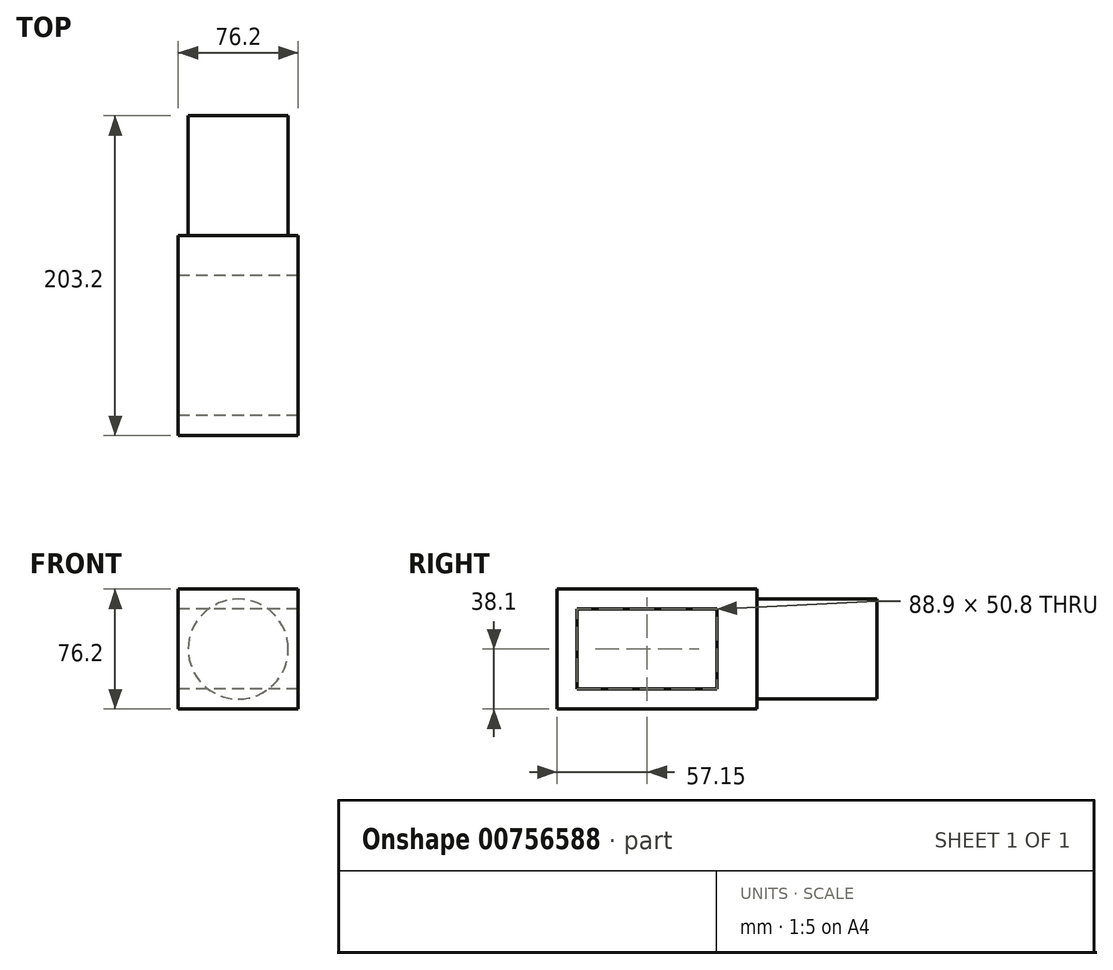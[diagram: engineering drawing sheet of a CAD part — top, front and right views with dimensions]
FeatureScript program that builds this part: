
annotation { "Feature Type Name" : "Feature", "Feature Type Description" : "" }
export const myFeature = defineFeature(function(context is Context, id is Id, definition is map)
    precondition{}
    {
        {
            var Q0;
            Q0=qCreatedBy(makeId("Right.planeOp"),FACE);
            var sketch = newSketch(context, id + "F0", { "sketchPlane" : qUnion([Q0])});
            skLineSegment(sketch, "E0.bottom", {"start": v(63.5, -38.1) * mm, "end": v(-63.5, -38.1) * mm});
            skLineSegment(sketch, "E0.top", {"start": v(63.5, 38.1) * mm, "end": v(-63.5, 38.1) * mm});
            skLineSegment(sketch, "E0.left", {"start": v(63.5, -38.1) * mm, "end": v(63.5, 38.1) * mm});
            skLineSegment(sketch, "E0.right", {"start": v(-63.5, -38.1) * mm, "end": v(-63.5, 38.1) * mm});
            skPoint(sketch, "E0.middle", {"position": v(0, 0) * mm});
            skSolve(sketch);
        }
        {
            var Q0;
            Q0 = qSketchRegion(id + "F0", true);
            extrude(context, id + "F1", {"entities" : qUnion([Q0]), "depth" : 76.2 * mm, "offsetDistance" : 25.4 * mm});
        }
        {
            var Q0;
            Q0=makeQuery(id+"F1.opExtrude","SWEPT_FACE",FACE,{"disambiguationData":[OSD([sQuery(id+"F0.wireOp",EDGE,"E0.left")])]});
            var sketch = newSketch(context, id + "F2", { "sketchPlane" : qUnion([Q0])});
            skLineSegment(sketch, "E1.0", {"start": v(0, -38.1) * mm, "end": v(0, 38.1) * mm});
            skLineSegment(sketch, "E2.0", {"start": v(-76.2, -38.1) * mm, "end": v(0, -38.1) * mm});
            skLineSegment(sketch, "E3.0", {"start": v(-76.2, -38.1) * mm, "end": v(-76.2, 38.1) * mm});
            skLineSegment(sketch, "E4.0", {"start": v(-76.2, 38.1) * mm, "end": v(0, 38.1) * mm});
            skCircle(sketch, "E5", {"center": v(-38.1, 0) * mm, "radius": 38.1 * mm});
            skPoint(sketch, "E5.first.point", {"position": v(0, 0) * mm});
            skPoint(sketch, "E5.second.point", {"position": v(-76.2, 0) * mm});
            skPoint(sketch, "E5.third.point", {"position": v(-38.1, -38.1) * mm});
            skCircle(sketch, "E6.0", {"center": v(-38.1, 0) * mm, "radius": 31.75 * mm});
            skSolve(sketch);
        }
        {
            var Q0;
            Q0=makeQuery(id+"F2.imprint","IMPRINT",FACE,{"disambiguationData":[TD([[makeQuery(id+"F2.imprint","IMPRINT",EDGE,{"derivedFrom":sQuery(id+"F2.wireOp",EDGE,"E6.0")}),1.0]])]});
            extrude(context, id + "F3", {"entities" : qUnion([Q0]), "operationType" : NewBodyOperationType.ADD, "depth" : 76.2 * mm, "offsetDistance" : 25.4 * mm});
        }
        {
            var Q0;
            Q0=makeQuery(id+"F1.opExtrude","CAP_FACE",FACE,{"disambiguationData":[OSD([sQuery(id+"F0.wireOp",EDGE,"E0.bottom"),sQuery(id+"F0.wireOp",EDGE,"E0.top"),sQuery(id+"F0.wireOp",EDGE,"E0.left"),sQuery(id+"F0.wireOp",EDGE,"E0.right")])],"isStart":true});
            var sketch = newSketch(context, id + "F4", { "sketchPlane" : qUnion([Q0])});
            skLineSegment(sketch, "E7.0", {"start": v(-63.5, -38.1) * mm, "end": v(-63.5, 38.1) * mm});
            skLineSegment(sketch, "E8.0", {"start": v(63.5, -38.1) * mm, "end": v(63.5, 38.1) * mm});
            skLineSegment(sketch, "E9.0", {"start": v(-63.5, -38.1) * mm, "end": v(63.5, -38.1) * mm});
            skLineSegment(sketch, "E10.0", {"start": v(-63.5, 38.1) * mm, "end": v(63.5, 38.1) * mm});
            skLineSegment(sketch, "E11", {"start": v(-38.1, 25.4) * mm, "end": v(-38.1, -25.4) * mm});
            skLineSegment(sketch, "E12", {"start": v(-38.1, -25.4) * mm, "end": v(50.8, -25.4) * mm});
            skLineSegment(sketch, "E13", {"start": v(50.8, -25.4) * mm, "end": v(50.8, 25.4) * mm});
            skLineSegment(sketch, "E14", {"start": v(50.8, 25.4) * mm, "end": v(-38.1, 25.4) * mm});
            skSolve(sketch);
        }
        {
            var Q0;
            Q0=makeQuery(id+"F4.imprint","IMPRINT",FACE,{"disambiguationData":[TD([[makeQuery(id+"F4.imprint","IMPRINT",EDGE,{"derivedFrom":sQuery(id+"F4.wireOp",EDGE,"E11")}),1.0]])]});
            extrude(context, id + "F5", {"entities" : qUnion([Q0]), "operationType" : NewBodyOperationType.REMOVE, "endBound" : BoundingType.THROUGH_ALL, "oppositeDirection" : true, "depth" : 25.4 * mm, "offsetDistance" : 25.4 * mm});
        }
    });
